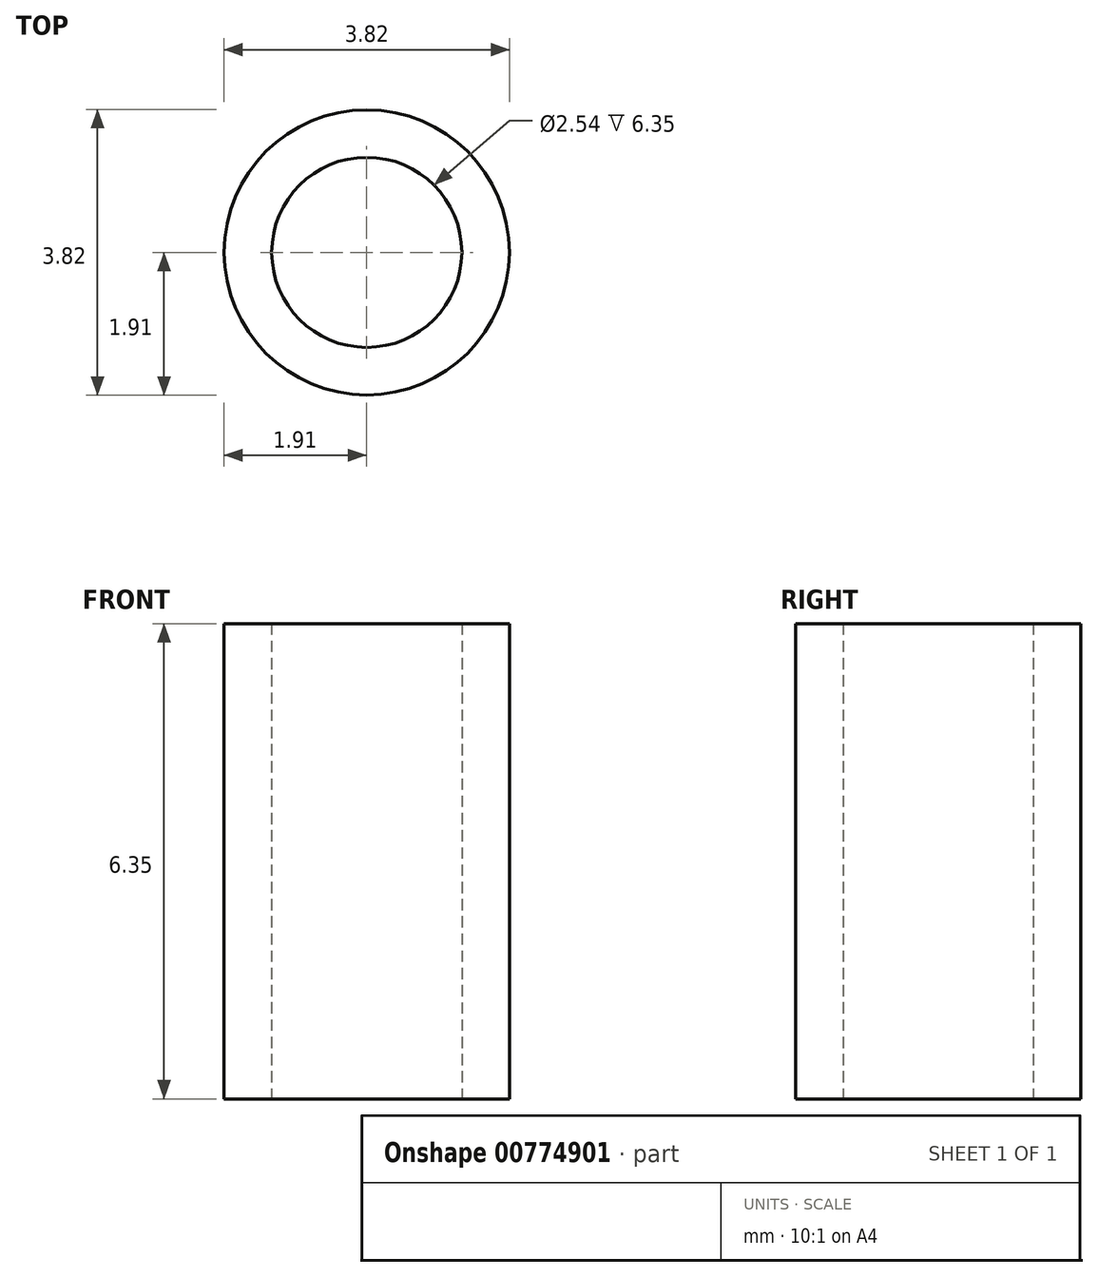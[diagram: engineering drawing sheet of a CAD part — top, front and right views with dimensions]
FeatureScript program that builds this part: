
annotation { "Feature Type Name" : "Feature", "Feature Type Description" : "" }
export const myFeature = defineFeature(function(context is Context, id is Id, definition is map)
    precondition{}
    {
        {
            var Q0;
            Q0=qCreatedBy(makeId("Top.planeOp"),FACE);
            var sketch = newSketch(context, id + "F0", { "sketchPlane" : qUnion([Q0])});
            skCircle(sketch, "E0", {"center": v(0, 0) * mm, "radius": 1.27 * mm});
            skCircle(sketch, "E1", {"center": v(0, 0) * mm, "radius": 1.9 * mm});
            skSolve(sketch);
        }
        {
            var Q0;
            Q0 = qSketchRegion(id + "F0", true);
            extrude(context, id + "F1", {"entities" : qUnion([Q0]), "depth" : 6.35 * mm, "offsetDistance" : 25.4 * mm});
        }
    });
